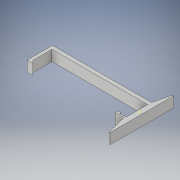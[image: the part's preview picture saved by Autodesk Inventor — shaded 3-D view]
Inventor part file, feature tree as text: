
AUTODESK INVENTOR PART (.ipt)
format: ipt  version: 2019 (Build 230136000, 136)  size: 177,664 bytes
history: native  units: mm
features: move_body x9, direct_edit x8, sketch x5, extrude x3, chamfer x1
ambient origin geometry x8: Origin, YZ Plane, XZ Plane, XY Plane, X Axis, Y Axis, Z Axis, Center Point
bodies: Solid1 (feature_tree)
feature tree (26):
  extrude  "Extrusion1"  Depth=20.0mm
  direct_edit  "Direct Edit1"
  direct_edit  "Direct Edit2"
  direct_edit  "Direct Edit3"
  sketch  "Sketch2"  dims[d2=20.0mm d3=1.0mm]
  sketch  "Sketch3"  dims[d4=20.0mm d5=1.0mm]
  extrude  "Extrusion2"  Depth=1.0mm
  direct_edit  "Direct Edit4"
  direct_edit  "Direct Edit5"
  extrude  "Extrusion3"  Depth=1.0mm
  chamfer  "Chamfer1"  Distance=5.0mm
  direct_edit  "Direct Edit6"
  direct_edit  "Direct Edit7"
  direct_edit  "Direct Edit8"
  sketch  "Sketch1"  dims[d0=6.0mm d1=20.0mm]
  sketch  "Sketch4"  dims[d6=1.5mm]
  sketch  "Sketch5"  dims[d7=2.5mm d8=5.0mm d9=3.0mm d10=2.5mm d11=60.0mm d12=10.0mm d13=0.0mm d14=0.0mm d15=0.0mm d16=-1.0mm d17=0.0mm d18=0.0mm d19=0.3mm d20=0.0mm d21=0.0mm d22=29.5mm d23=0.0mm d24=0.0mm d25=2.0mm d26=2.0mm d27=15.0mm d28=0.0mm d29=0.0mm d30=0.0mm d31=1.0mm d32=0.0mm d33=0.0mm d34=7.0mm d35=2.0mm d36=2.5mm d37=0.0mm d38=2.0mm d39=2.0mm d40=45.0deg d41=0.0mm d42=0.0mm d43=-2.0mm d44=0.0mm d45=0.0mm d46=0.5mm d47=0.0mm d48=0.0mm d49=1.0mm]
  move_body  "Move1"
  move_body  "Move2"
  move_body  "Move3"
  move_body  "Move4"
  move_body  "Move5"
  move_body  "Move6"
  move_body  "Move7"
  move_body  "Move8"
  move_body  "Move9"
